# Revit family: TRP
name_source: partatom
category: Lighting Fixtures
revit_build: Autodesk Revit MEP 2012 (Build: 20110309_2315(x64)
units: mm (PartAtom-declared; Revit-internal decimal feet)

## types (5) — shared parameters
Apparent Load = 0 VA
Color Filter = 16777215
Default Elevation = 48"
Description = TRP Trapezoid HID/CFL
Dimming Lamp Color Temperature Shift = <None>
Emit Shape Visible in Rendering = No
Emit from Rectangle Length = 12"
Emit from Rectangle Width = 6"
Lamp = LED
Load Classification = Lighting
Manufacturer = Hubbell Outdoor
Manufacturer Fax = 864-678-1065
Model = TRP1
Opal lens = Etched Glass
Photometric Web File = TRP 150PX WT.ies
Product Documentation Link = http://cdn.hubbelloutdoor.com
Product Page URL = http://www.hubbelloutdoor.com
Tilt Angle = 90.00°
URL = http://www.hubbelloutdoor.com
Voltage = 120 V
Watt = 15 W
Wattage Comments = 15W/20W/30W

## per-type parameters (varying)
| type | Finish |
| TRP BD | Bronze |
| TRP BL | Black |
| TRP WH | White |
| TRP PL | Platinum |
| TRP BRZ | Gray |

## geometry (parser evidence)
native form markers: Blend x6, Sweep x1
no freeform markers — native parametric forms only
